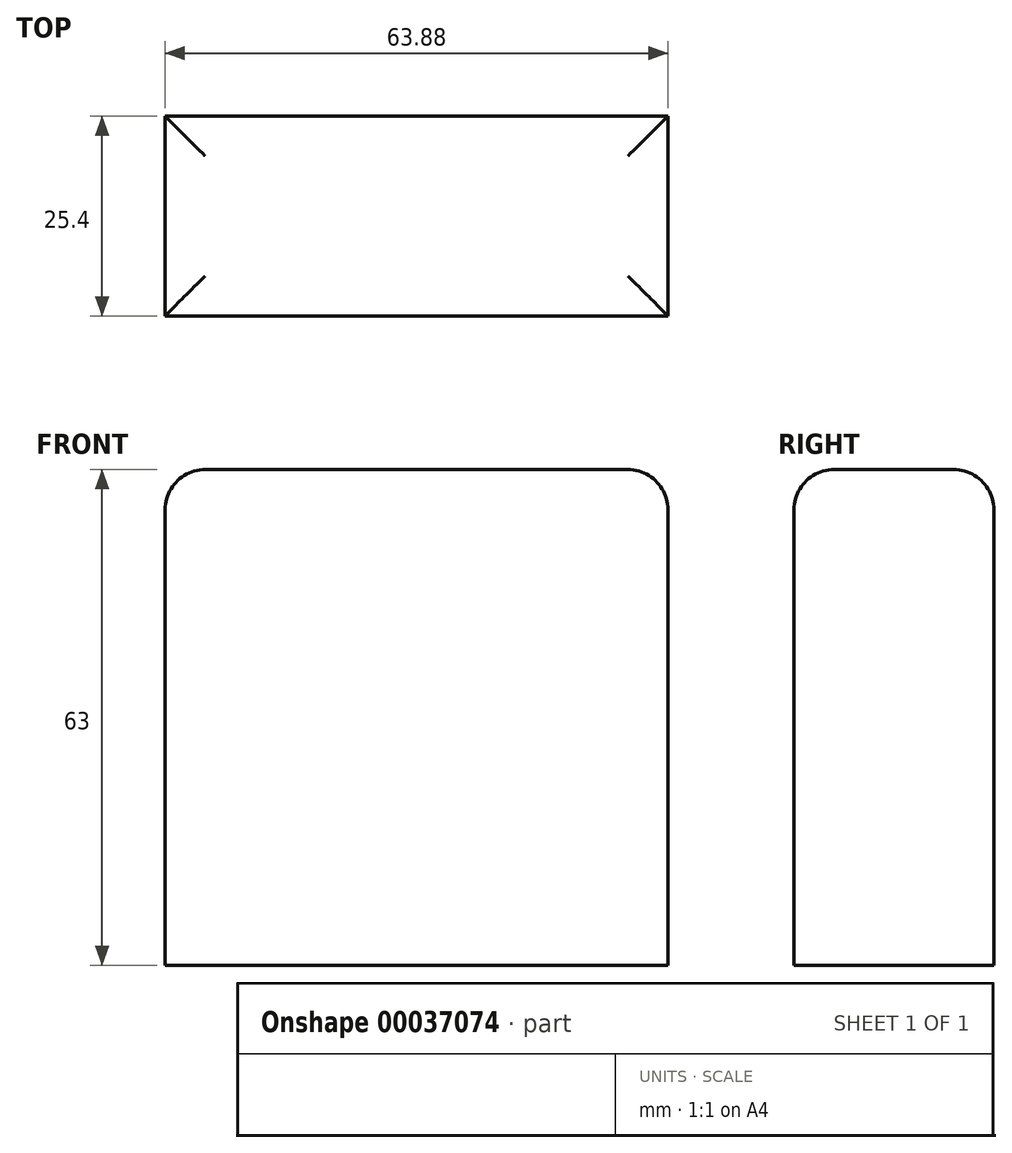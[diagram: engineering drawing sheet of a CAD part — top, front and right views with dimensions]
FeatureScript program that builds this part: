
annotation { "Feature Type Name" : "Feature", "Feature Type Description" : "" }
export const myFeature = defineFeature(function(context is Context, id is Id, definition is map)
    precondition{}
    {
        {
            var Q0;
            Q0=qCreatedBy(makeId("Front.planeOp"),FACE);
            var sketch = newSketch(context, id + "F0", { "sketchPlane" : qUnion([Q0])});
            skLineSegment(sketch, "E0.bottom", {"start": v(-34.46, -7.22) * mm, "end": v(29.42, -7.22) * mm});
            skLineSegment(sketch, "E0.top", {"start": v(-34.46, 55.78) * mm, "end": v(29.42, 55.78) * mm});
            skLineSegment(sketch, "E0.left", {"start": v(-34.46, -7.22) * mm, "end": v(-34.46, 55.78) * mm});
            skLineSegment(sketch, "E0.right", {"start": v(29.42, -7.22) * mm, "end": v(29.42, 55.78) * mm});
            skSolve(sketch);
        }
        {
            var Q0;
            Q0 = qSketchRegion(id + "F0", true);
            extrude(context, id + "F1", {"entities" : qUnion([Q0]), "depth" : 25.4 * mm});
        }
        {
            var Q0;
            Q0=makeQuery(id+"F1.opExtrude","SWEPT_EDGE",EDGE,{"disambiguationData":[OSD([sQuery(id+"F0.wireOp",EDGE,"E0.top"),sQuery(id+"F0.wireOp",EDGE,"E0.left")])]});
            var Q1;
            Q1=makeQuery(id+"F1.opExtrude","SWEPT_EDGE",EDGE,{"disambiguationData":[OSD([sQuery(id+"F0.wireOp",EDGE,"E0.top"),sQuery(id+"F0.wireOp",EDGE,"E0.right")])]});
            var Q2;
            Q2=makeQuery(id+"F1.opExtrude","CAP_EDGE",EDGE,{"disambiguationData":[OSD([sQuery(id+"F0.wireOp",EDGE,"E0.top")])],"isStart":false});
            var Q3;
            Q3=makeQuery(id+"F1.opExtrude","CAP_EDGE",EDGE,{"disambiguationData":[OSD([sQuery(id+"F0.wireOp",EDGE,"E0.top")])],"isStart":true});
            fillet(context, id + "F2", {"entities" : qUnion([Q0, Q1, Q2, Q3]), "radius" : 5.08 * mm, "tangentPropagation" : true, "allowEdgeOverflow" : false});
        }
    });
